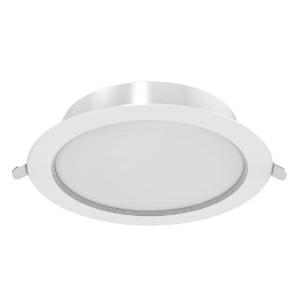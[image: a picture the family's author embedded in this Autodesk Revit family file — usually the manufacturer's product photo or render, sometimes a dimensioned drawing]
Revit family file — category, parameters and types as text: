
# Revit family: leddownlightco-e_rd125-14w-840_540001291200
name_source: partatom
category: Leuchten
revit_build: Autodesk Revit 2016 (Build: 20190508_0715(x64)
units: mm (PartAtom-declared; Revit-internal decimal feet)

## family parameters
Basisbauteil = Fläche
Beim Laden mit Abzugskörper schneiden = Nein
Bemaßung runder Anschluss = Durchmesser verwenden
Gemeinsam genutzt = Nein
Lichtquelle = Nein
Raumberechnungspunkt = Nein
Teiletyp = Normal

## types (1)
- LEDDownlightCo-E Rd125-14W-840 (1 x LED, 1260 lm)
    Approval mark = CE
    Beschreibung = Stylish and compact LED downlight. Sturdy full metal housing. Integrated driver for easier installation. Low height of only 35mm. IP44 on light emitting side.
    CIE Flux Codes = 50 81 96 100 100
    Control Gear = Electronic ballast
    Height = 0 mm  [stored 0 ft]
    Hersteller = OPPLE
    Lamp Light Flux = 1260 lm
    Lamp count = 1
    Lampe = 1 x LED
    Length = 100 mm  [stored 0.328084 ft]
    Luminous efficacy = 90 lm/W
    ModVariant = Nein
    Modell = 540001291200
    Mounting Place = Ceiling
    Mounting Type = Recessed
    Number of Poles = 1
    OnlyDefault = Ja
    Power Factor = 1
    Product Name = LEDDownlightCo-E Rd125-14W-840
    Product group = Downlight Compact
    ProductGroupID = 406
    Protection Class = Protection class II
    Protection Degree = IP 44
    RLX_Detail_Level = 1
    RlxData = <blob elided: 108689 chars, md5=753ef106>
    Scheinlast = 14 VA
    Socket = socket
    Standby Power = 0 W
    System Light Flux = 1260 lm
    System Power = 14 W
    Typenbild = 540001291200.jpg
    Typenkommentare = Product without accessories
    URL = http://relux.com
    VarID = ---
    Voltage = 230 V
    Voltage Range = 220-240 V
    Vorgabe-Ansicht = 1800 mm
    Weight = 0.00 kg
    Width = 100 mm  [stored 0.328084 ft]

note: [stored X ft] marks values corroborated as IEEE doubles in the binary element streams (Revit-internal decimal feet)

## geometry (parser evidence)
native form markers: Sweep x11
no freeform markers — native parametric forms only
